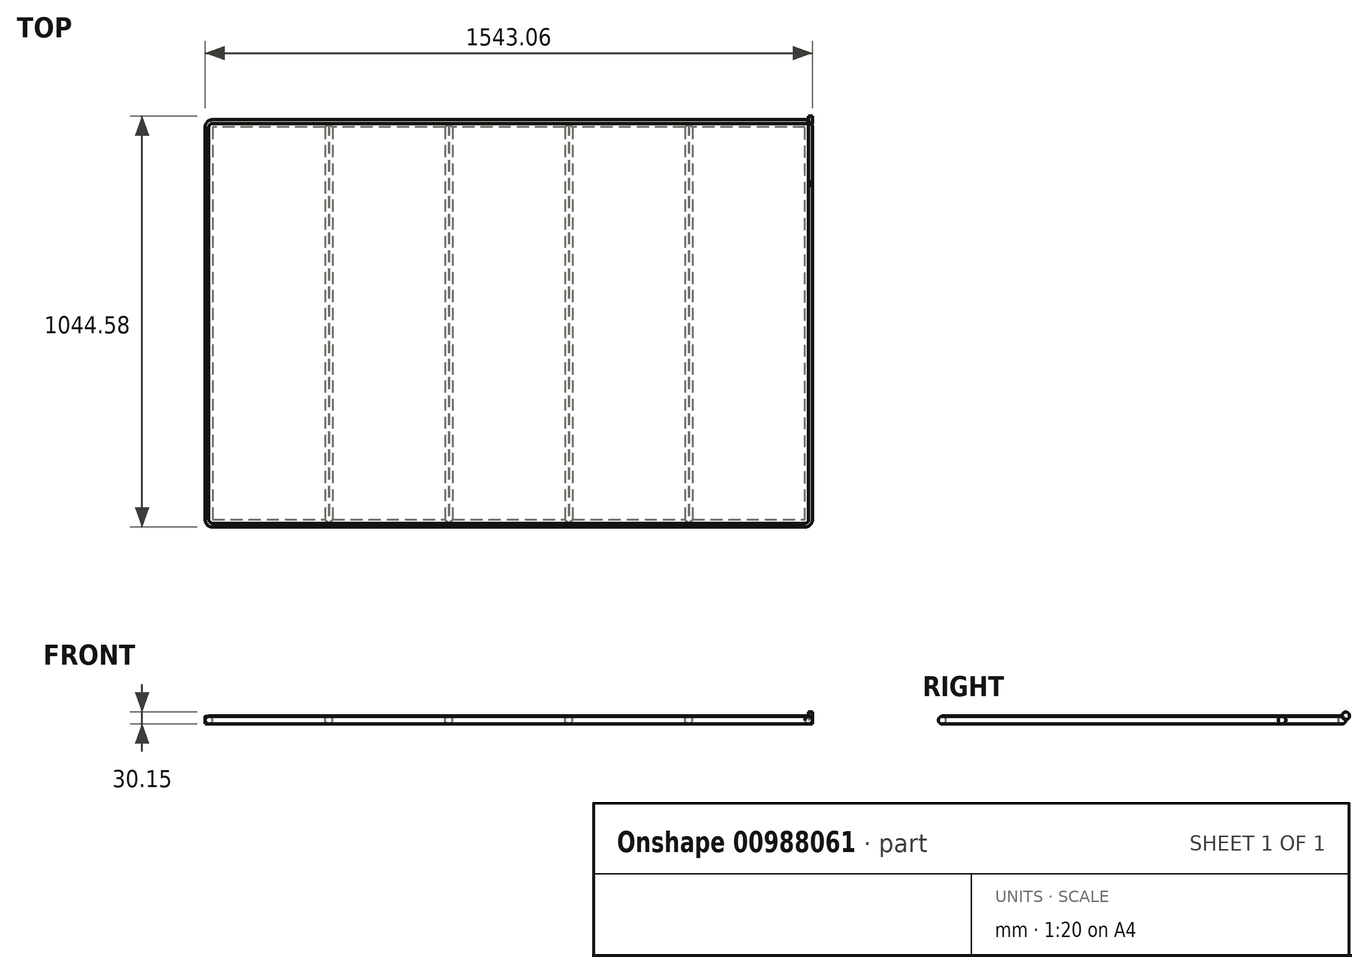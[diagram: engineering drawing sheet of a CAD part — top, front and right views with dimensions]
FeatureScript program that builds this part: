
annotation { "Feature Type Name" : "Feature", "Feature Type Description" : "" }
export const myFeature = defineFeature(function(context is Context, id is Id, definition is map)
    precondition{}
    {
        {
            var Q0;
            Q0=qCreatedBy(makeId("Top.planeOp"),FACE);
            var sketch = newSketch(context, id + "F0", { "sketchPlane" : qUnion([Q0])});
            skLineSegment(sketch, "E0.left", {"start": v(0, -152.4) * mm, "end": v(0, -863.6) * mm});
            skLineSegment(sketch, "E1.direction1", {"start": v(0, -330.2) * mm, "end": v(25.4, -330.2) * mm, "construction": true});
            skLineSegment(sketch, "E1.direction2", {"start": v(0, -330.2) * mm, "end": v(0, -668.78) * mm, "construction": true});
            skLineSegment(sketch, "E2.1.0.0", {"start": v(304.8, 0) * mm, "end": v(304.8, -1016) * mm});
            skLineSegment(sketch, "E2.2.0.0", {"start": v(609.6, 0) * mm, "end": v(609.6, -1016) * mm});
            skLineSegment(sketch, "E2.3.0.0", {"start": v(914.4, 0) * mm, "end": v(914.4, -1016) * mm});
            skLineSegment(sketch, "E2.4.0.0", {"start": v(1219.2, 0) * mm, "end": v(1219.2, -1016) * mm});
            skCircle(sketch, "E3", {"center": v(304.8, 0) * mm, "radius": 9.53 * mm});
            skCircle(sketch, "E4", {"center": v(609.6, 0) * mm, "radius": 9.53 * mm});
            skCircle(sketch, "E5", {"center": v(914.4, 0) * mm, "radius": 9.53 * mm});
            skCircle(sketch, "E6", {"center": v(1219.2, 0) * mm, "radius": 9.53 * mm});
            skCircle(sketch, "E7", {"center": v(1524, -508) * mm, "radius": 9.53 * mm});
            skCircle(sketch, "E8", {"center": v(1219.2, -1016) * mm, "radius": 9.52 * mm});
            skCircle(sketch, "E9", {"center": v(914.4, -1016) * mm, "radius": 9.52 * mm});
            skCircle(sketch, "E10", {"center": v(609.6, -1016) * mm, "radius": 9.52 * mm});
            skCircle(sketch, "E11", {"center": v(304.8, -1016) * mm, "radius": 9.53 * mm});
            skCircle(sketch, "E12", {"center": v(0, -508) * mm, "radius": 9.53 * mm});
            skLineSegment(sketch, "E13", {"start": v(0, -1006.48) * mm, "end": v(0, -9.53) * mm});
            skLineSegment(sketch, "E14", {"start": v(9.53, 0) * mm, "end": v(1514.48, 0) * mm});
            skLineSegment(sketch, "E15", {"start": v(1524, -9.53) * mm, "end": v(1524, -1006.48) * mm});
            skLineSegment(sketch, "E16", {"start": v(1514.48, -1016) * mm, "end": v(9.53, -1016) * mm});
            skPoint(sketch, "E17.visualSharp", {"position": v(0, 0) * mm});
            skArc(sketch, "E17.filletArc", {"start": v(9.53, 0) * mm, "mid": v(2.79, -2.79) * mm, "end": v(0, -9.53) * mm});
            skPoint(sketch, "E18.visualSharp", {"position": v(1524, 0) * mm});
            skArc(sketch, "E18.filletArc", {"start": v(1524, -9.53) * mm, "mid": v(1521.21, -2.79) * mm, "end": v(1514.48, 0) * mm});
            skPoint(sketch, "E19.visualSharp", {"position": v(1524, -1016) * mm});
            skArc(sketch, "E19.filletArc", {"start": v(1514.48, -1016) * mm, "mid": v(1521.21, -1013.21) * mm, "end": v(1524, -1006.48) * mm});
            skPoint(sketch, "E20.visualSharp", {"position": v(0, -1016) * mm});
            skCircle(sketch, "E21", {"center": v(2.79, -2.79) * mm, "radius": 9.53 * mm});
            skCircle(sketch, "E22", {"center": v(1521.21, -2.79) * mm, "radius": 9.53 * mm});
            skCircle(sketch, "E23", {"center": v(1521.21, -1013.21) * mm, "radius": 9.53 * mm});
            skCircle(sketch, "E24", {"center": v(2.79, -1013.21) * mm, "radius": 9.53 * mm});
            skArc(sketch, "E25.filletArc", {"start": v(0, -1006.48) * mm, "mid": v(2.79, -1013.21) * mm, "end": v(9.53, -1016) * mm});
            skSolve(sketch);
        }
        {
            var Q0;
            Q0=qCreatedBy(makeId("Front.planeOp"),FACE);
            cPlane(context, id + "F1", {"entities" : qUnion([Q0]), "cplaneType" : CPlaneType.OFFSET, "offset" : 609.6 * mm, "width" : 152.4 * mm, "height" : 152.4 * mm});
        }
        {
            var Q0;
            Q0=qCreatedBy(id+"F1.planeOp",FACE);
            var sketch = newSketch(context, id + "F2", { "sketchPlane" : qUnion([Q0])});
            skCircle(sketch, "E26", {"center": v(0, 0) * mm, "radius": 9.53 * mm});
            skCircle(sketch, "E27.1.0.0", {"center": v(304.8, 0) * mm, "radius": 9.53 * mm});
            skCircle(sketch, "E27.2.0.0", {"center": v(609.6, 0) * mm, "radius": 9.53 * mm});
            skCircle(sketch, "E27.3.0.0", {"center": v(914.4, 0) * mm, "radius": 9.53 * mm});
            skCircle(sketch, "E27.4.0.0", {"center": v(1219.2, 0) * mm, "radius": 9.53 * mm});
            skLineSegment(sketch, "E27.direction1", {"start": v(0, 0) * mm, "end": v(304.8, 0) * mm, "construction": true});
            skSolve(sketch);
        }
        {
            var Q0;
            Q0=makeQuery(id+"F2.imprint","IMPRINT",FACE,{"disambiguationData":[TD([[makeQuery(id+"F2.imprint","IMPRINT",EDGE,{"derivedFrom":sQuery(id+"F2.wireOp",EDGE,"E26")}),1.0]])]});
            var Q1;
            Q1=sQuery(id+"F0.wireOp",EDGE,"E13");
            var Q2;
            Q2=sQuery(id+"F0.wireOp",EDGE,"E20.filletArc");
            var Q3;
            Q3=sQuery(id+"F0.wireOp",EDGE,"E17.filletArc");
            var Q4;
            Q4=sQuery(id+"F0.wireOp",EDGE,"E14");
            var Q5;
            Q5=sQuery(id+"F0.wireOp",EDGE,"E18.filletArc");
            var Q6;
            Q6=sQuery(id+"F0.wireOp",EDGE,"E15");
            var Q7;
            Q7=sQuery(id+"F0.wireOp",EDGE,"E19.filletArc");
            var Q8;
            Q8=sQuery(id+"F0.wireOp",EDGE,"E16");
            var Q9;
            Q9=sQuery(id+"F0.wireOp",EDGE,"E25.filletArc");
            sweep(context, id + "F3", {"profiles" : qUnion([Q0]), "path" : qUnion([Q1, Q2, Q3, Q4, Q5, Q6, Q7, Q8, Q9])});
        }
        {
            var Q0;
            Q0=makeQuery(id+"F2.imprint","IMPRINT",FACE,{"disambiguationData":[TD([[makeQuery(id+"F2.imprint","IMPRINT",EDGE,{"derivedFrom":sQuery(id+"F2.wireOp",EDGE,"E27.1.0.0")}),1.0]])]});
            var Q1;
            Q1=makeQuery(id+"F2.imprint","IMPRINT",FACE,{"disambiguationData":[TD([[makeQuery(id+"F2.imprint","IMPRINT",EDGE,{"derivedFrom":sQuery(id+"F2.wireOp",EDGE,"E27.2.0.0")}),1.0]])]});
            var Q2;
            Q2=makeQuery(id+"F2.imprint","IMPRINT",FACE,{"disambiguationData":[TD([[makeQuery(id+"F2.imprint","IMPRINT",EDGE,{"derivedFrom":sQuery(id+"F2.wireOp",EDGE,"E27.3.0.0")}),1.0]])]});
            var Q3;
            Q3=makeQuery(id+"F2.imprint","IMPRINT",FACE,{"disambiguationData":[TD([[makeQuery(id+"F2.imprint","IMPRINT",EDGE,{"derivedFrom":sQuery(id+"F2.wireOp",EDGE,"E27.4.0.0")}),1.0]])]});
            var Q4;
            Q4=sQuery(id+"F0.wireOp",EDGE,"E2.1.0.0");
            sweep(context, id + "F4", {"operationType" : NewBodyOperationType.ADD, "profiles" : qUnion([Q0, Q1, Q2, Q3]), "path" : qUnion([Q4])});
        }
        {
            var Q0;
            Q0=qCreatedBy(makeId("Top.planeOp"),FACE);
            cPlane(context, id + "F5", {"entities" : qUnion([Q0]), "cplaneType" : CPlaneType.OFFSET, "offset" : 9.5 * mm, "width" : 152.4 * mm, "height" : 152.4 * mm});
        }
        {
            var Q0;
            Q0=qCreatedBy(id+"F5.planeOp",FACE);
            var sketch = newSketch(context, id + "F6", { "sketchPlane" : qUnion([Q0])});
            skPoint(sketch, "E28.visualSharp", {"position": v(0, 0) * mm});
            skPoint(sketch, "E29.visualSharp", {"position": v(1524, 0) * mm});
            skPoint(sketch, "E30.visualSharp", {"position": v(1524, -1016) * mm});
            skPoint(sketch, "E31.visualSharp", {"position": v(0, -1016) * mm});
            skLineSegment(sketch, "E32", {"start": v(0, -1006.48) * mm, "end": v(0, -9.53) * mm});
            skLineSegment(sketch, "E33", {"start": v(9.53, 0) * mm, "end": v(1514.48, 0) * mm});
            skLineSegment(sketch, "E34", {"start": v(1524, -9.53) * mm, "end": v(1524, -1006.48) * mm});
            skLineSegment(sketch, "E35", {"start": v(1514.48, -1016) * mm, "end": v(9.53, -1016) * mm});
            skArc(sketch, "E36.filletArc", {"start": v(9.53, 0) * mm, "mid": v(2.79, -2.79) * mm, "end": v(0, -9.53) * mm});
            skArc(sketch, "E37.filletArc", {"start": v(1524, -9.53) * mm, "mid": v(1521.21, -2.79) * mm, "end": v(1514.48, 0) * mm});
            skArc(sketch, "E38.filletArc", {"start": v(1514.48, -1016) * mm, "mid": v(1521.21, -1013.21) * mm, "end": v(1524, -1006.48) * mm});
            skArc(sketch, "E39.filletArc", {"start": v(0, -1006.48) * mm, "mid": v(2.79, -1013.21) * mm, "end": v(9.53, -1016) * mm});
            skSolve(sketch);
        }
        {
            var Q0;
            Q0=qSketchRegion(id+"F6",true);
            extrude(context, id + "F7", {"entities" : qUnion([Q0]), "operationType" : NewBodyOperationType.ADD, "depth" : 1.59 * mm, "offsetDistance" : 25.4 * mm});
        }
        {
            var Q0;
            Q0=qCreatedBy(makeId("Right.planeOp"),FACE);
            cPlane(context, id + "F8", {"entities" : qUnion([Q0]), "cplaneType" : CPlaneType.OFFSET, "offset" : 1524 * mm, "width" : 152.4 * mm, "height" : 152.4 * mm});
        }
        {
            var Q0;
            Q0=qCreatedBy(id+"F8.planeOp",FACE);
            var sketch = newSketch(context, id + "F9", { "sketchPlane" : qUnion([Q0])});
            skLineSegment(sketch, "E40", {"start": v(0, 0) * mm, "end": v(-152.4, 0) * mm, "construction": true});
            skCircle(sketch, "E41", {"center": v(-152.4, 0) * mm, "radius": 9.53 * mm});
            skLineSegment(sketch, "E42", {"start": v(0, 0) * mm, "end": v(9.53, 0) * mm, "construction": true});
            skLineSegment(sketch, "E43", {"start": v(9.53, 0) * mm, "end": v(9.53, 9.53) * mm, "construction": true});
            skLineSegment(sketch, "E44", {"start": v(9.53, 9.53) * mm, "end": v(9.53, 11.1) * mm, "construction": true});
            skCircle(sketch, "E45", {"center": v(9.53, 11.1) * mm, "radius": 9.53 * mm});
            skSolve(sketch);
        }
        {
            var Q0;
            Q0 = qSketchRegion(id + "F9", true);
            var Q1;
            Q1 = qConstructionFilter(qBodyType(qCreatedBy(id + "F9" ,EDGE), BodyType.WIRE), ConstructionObject.NO);
            extrude(context, id + "F10", {"entities" : qUnion([Q0]), "operationType" : NewBodyOperationType.ADD, "surfaceEntities" : qUnion([Q1]), "depth" : 9.52 * mm, "offsetDistance" : 25.4 * mm});
        }
        {
            var Q0;
            Q0=qCreatedBy(makeId("Right.planeOp"),FACE);
            var sketch = newSketch(context, id + "F11", { "sketchPlane" : qUnion([Q0])});
            skLineSegment(sketch, "E46", {"start": v(0, 0) * mm, "end": v(-152.4, 0) * mm, "construction": true});
            skCircle(sketch, "E47", {"center": v(-152.4, 0) * mm, "radius": 9.53 * mm});
            skSolve(sketch);
        }
        {
            var Q0;
            Q0 = qSketchRegion(id + "F11", true);
            extrude(context, id + "F12", {"entities" : qUnion([Q0]), "operationType" : NewBodyOperationType.ADD, "oppositeDirection" : true, "depth" : 9.52 * mm, "offsetDistance" : 25.4 * mm});
        }
    });
